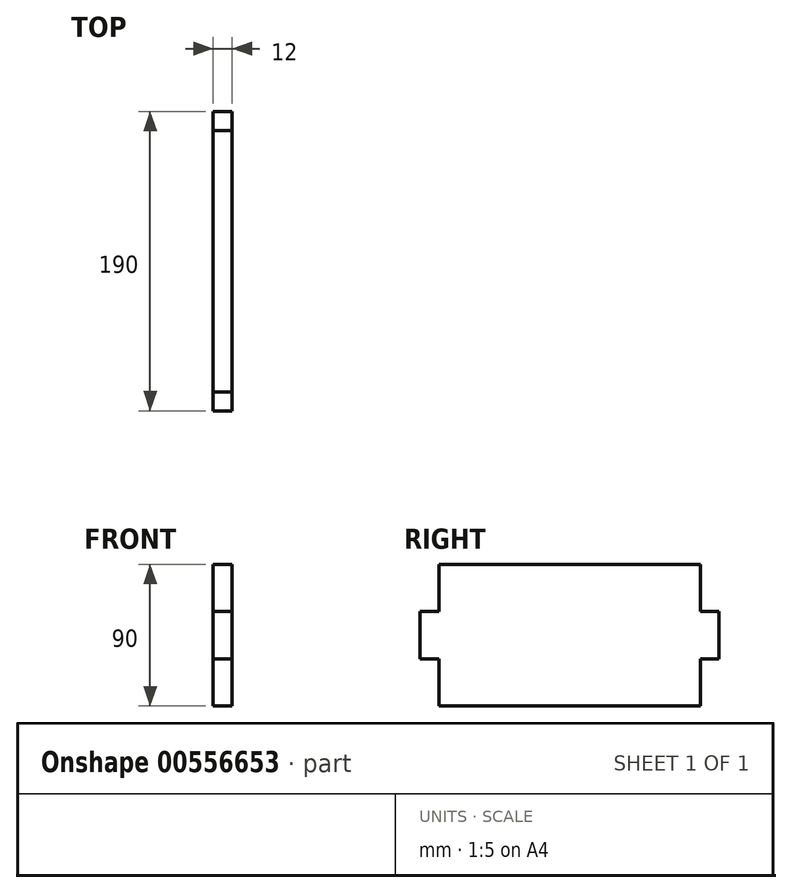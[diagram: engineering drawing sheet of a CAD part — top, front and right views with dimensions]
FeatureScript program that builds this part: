
annotation { "Feature Type Name" : "Feature", "Feature Type Description" : "" }
export const myFeature = defineFeature(function(context is Context, id is Id, definition is map)
    precondition{}
    {
        {
            var Q0;
            Q0=qCreatedBy(makeId("Right.planeOp"),FACE);
            var sketch = newSketch(context, id + "F0", { "sketchPlane" : qUnion([Q0])});
            skLineSegment(sketch, "E0", {"start": v(0, 0) * mm, "end": v(0, 30) * mm});
            skLineSegment(sketch, "E1", {"start": v(0, 30) * mm, "end": v(-12, 30) * mm});
            skLineSegment(sketch, "E2", {"start": v(-12, 30) * mm, "end": v(-12, 60) * mm});
            skLineSegment(sketch, "E3", {"start": v(-12, 60) * mm, "end": v(0, 60) * mm});
            skLineSegment(sketch, "E4", {"start": v(0, 60) * mm, "end": v(0, 90) * mm});
            skLineSegment(sketch, "E5", {"start": v(0, 90) * mm, "end": v(83, 90) * mm});
            skLineSegment(sketch, "E6", {"start": v(83, 90) * mm, "end": v(83, 0) * mm, "construction": true});
            skLineSegment(sketch, "E7", {"start": v(83, 0) * mm, "end": v(0, 0) * mm});
            skLineSegment(sketch, "E8.MirrorCS", {"start": v(166, 30) * mm, "end": v(178, 30) * mm});
            skLineSegment(sketch, "E9.MirrorCS", {"start": v(178, 30) * mm, "end": v(178, 60) * mm});
            skLineSegment(sketch, "E10.MirrorCS", {"start": v(178, 60) * mm, "end": v(166, 60) * mm});
            skLineSegment(sketch, "E11.MirrorCS", {"start": v(166, 60) * mm, "end": v(166, 90) * mm});
            skLineSegment(sketch, "E12.MirrorCS", {"start": v(166, 0) * mm, "end": v(166, 30) * mm});
            skLineSegment(sketch, "E13.MirrorCS", {"start": v(166, 90) * mm, "end": v(83, 90) * mm});
            skLineSegment(sketch, "E14.MirrorCS", {"start": v(83, 0) * mm, "end": v(166, 0) * mm});
            skSolve(sketch);
        }
        {
            var Q0;
            Q0 = qSketchRegion(id + "F0", true);
            extrude(context, id + "F1", {"entities" : qUnion([Q0]), "endBound" : BoundingType.SYMMETRIC, "depth" : 12 * mm, "offsetDistance" : 25 * mm});
        }
    });
